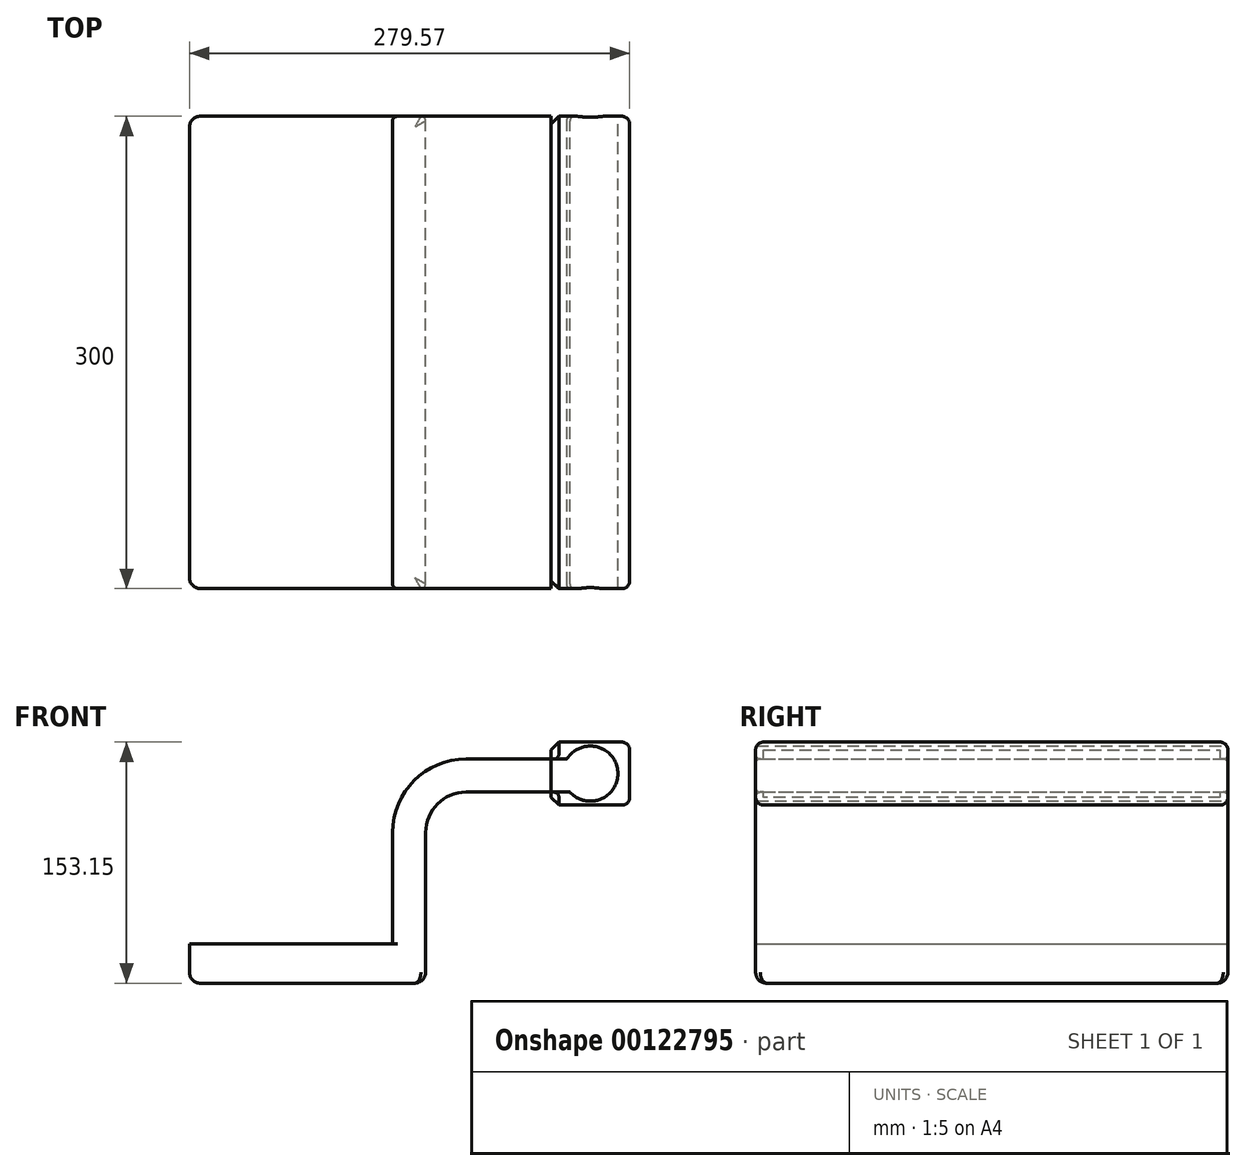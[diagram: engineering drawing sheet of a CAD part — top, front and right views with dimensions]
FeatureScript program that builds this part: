
annotation { "Feature Type Name" : "Feature", "Feature Type Description" : "" }
export const myFeature = defineFeature(function(context is Context, id is Id, definition is map)
    precondition{}
    {
        {
            var Q0;
            Q0=qCreatedBy(makeId("Front.planeOp"),FACE);
            var sketch = newSketch(context, id + "F0", { "sketchPlane" : qUnion([Q0])});
            skLineSegment(sketch, "E0.bottom", {"start": v(20.04, -25.24) * mm, "end": v(-129.96, -25.24) * mm});
            skLineSegment(sketch, "E0.top", {"start": v(20.04, -50.24) * mm, "end": v(-129.96, -50.24) * mm});
            skLineSegment(sketch, "E0.left", {"start": v(20.04, -25.24) * mm, "end": v(20.04, -50.24) * mm});
            skLineSegment(sketch, "E0.right", {"start": v(-129.96, -25.24) * mm, "end": v(-129.96, -50.24) * mm});
            skLineSegment(sketch, "E1.bottom", {"start": v(149.61, 102.9) * mm, "end": v(99.61, 102.9) * mm});
            skLineSegment(sketch, "E1.top", {"start": v(149.61, 62.9) * mm, "end": v(99.61, 62.9) * mm});
            skLineSegment(sketch, "E1.left", {"start": v(149.61, 102.9) * mm, "end": v(149.61, 62.9) * mm});
            skLineSegment(sketch, "E1.right", {"start": v(99.61, 102.9) * mm, "end": v(99.61, 62.9) * mm});
            skLineSegment(sketch, "E2", {"start": v(20.04, -25.24) * mm, "end": v(20.04, 45.54) * mm});
            skArc(sketch, "E3", {"start": v(20.04, 45.54) * mm, "mid": v(27.53, 63.63) * mm, "end": v(45.62, 71.13) * mm});
            skLineSegment(sketch, "E4", {"start": v(45.62, 71.13) * mm, "end": v(115.1, 71.13) * mm});
            skLineSegment(sketch, "E5.0", {"start": v(45.62, 92.13) * mm, "end": v(115.1, 92.13) * mm});
            skArc(sketch, "E5.1", {"start": v(-0.96, 45.54) * mm, "mid": v(12.68, 78.48) * mm, "end": v(45.62, 92.13) * mm});
            skLineSegment(sketch, "E5.2", {"start": v(-0.96, -25.24) * mm, "end": v(-0.96, 45.54) * mm});
            skArc(sketch, "E6", {"start": v(45.62, 92.13) * mm, "mid": v(-59.98, 60.08) * mm, "end": v(-129.96, -25.24) * mm});
            skCircle(sketch, "E7", {"center": v(124.61, 82.9) * mm, "radius": 17.5 * mm});
            skSolve(sketch);
        }
        {
            var Q0;
            Q0=makeQuery(id+"F0.imprint","IMPRINT",FACE,{"disambiguationData":[TD([[makeQuery(id+"F0.imprint","IMPRINT",EDGE,{"derivedFrom":sQuery(id+"F0.wireOp",EDGE,"E0.top")}),-1.0]])]});
            extrude(context, id + "F1", {"entities" : qUnion([Q0]), "depth" : 300 * mm});
        }
        {
            var Q0;
            Q0=makeQuery(id+"F0.imprint","IMPRINT",FACE,{"disambiguationData":[TD([[makeQuery(id+"F0.imprint","IMPRINT",EDGE,{"derivedFrom":sQuery(id+"F0.wireOp",EDGE,"E5.1")}),1.0]])]});
            var Q1;
            {var subQ2=sQuery(id+"F0.wireOp",EDGE,"E2");Q1=makeQuery(id+"F0.imprint","IMPRINT",FACE,{"disambiguationData":[TD([[makeQuery(id+"F0.imprint","IMPRINT",EDGE,{"derivedFrom":subQ2}),1.0]])]});}
            var Q2;
            {var subQ1=sQuery(id+"F0.wireOp",EDGE,"E1.bottom");Q2=makeQuery(id+"F0.imprint","IMPRINT",FACE,{"disambiguationData":[TD([[makeQuery(id+"F0.imprint","IMPRINT",EDGE,{"derivedFrom":subQ1}),1.0]])]});}
            extrude(context, id + "F2", {"entities" : qUnion([Q0, Q1, Q2]), "operationType" : NewBodyOperationType.ADD, "depth" : 300 * mm});
        }
        {
            var Q0;
            Q0=makeQuery(id+"F2.opExtrude","CAP_EDGE",EDGE,{"disambiguationData":[OSD([sQuery(id+"F0.wireOp",EDGE,"E1.left")])],"isStart":false});
            var Q1;
            Q1=makeQuery(id+"F2.opExtrude","CAP_EDGE",EDGE,{"disambiguationData":[OSD([sQuery(id+"F0.wireOp",EDGE,"E1.left")])],"isStart":true});
            var Q2;
            Q2=makeQuery(id+"F2.opExtrude","SWEPT_EDGE",EDGE,{"disambiguationData":[OSD([sQuery(id+"F0.wireOp",EDGE,"E1.bottom"),sQuery(id+"F0.wireOp",EDGE,"E1.left")])]});
            var Q3;
            Q3=makeQuery(id+"F2.opExtrude","SWEPT_EDGE",EDGE,{"disambiguationData":[OSD([sQuery(id+"F0.wireOp",EDGE,"E1.top"),sQuery(id+"F0.wireOp",EDGE,"E1.left")])]});
            var Q4;
            Q4=makeQuery(id+"F2.opExtrude","CAP_EDGE",EDGE,{"disambiguationData":[OSD([sQuery(id+"F0.wireOp",EDGE,"E1.bottom")])],"isStart":false});
            var Q5;
            Q5=makeQuery(id+"F2.opExtrude","CAP_EDGE",EDGE,{"disambiguationData":[OSD([sQuery(id+"F0.wireOp",EDGE,"E1.top")])],"isStart":false});
            var Q6;
            Q6=makeQuery(id+"F2.opExtrude","CAP_EDGE",EDGE,{"disambiguationData":[OSD([sQuery(id+"F0.wireOp",EDGE,"E1.bottom")])],"isStart":true});
            var Q7;
            Q7=makeQuery(id+"F2.opExtrude","CAP_EDGE",EDGE,{"disambiguationData":[OSD([sQuery(id+"F0.wireOp",EDGE,"E1.top")])],"isStart":true});
            fillet(context, id + "F3", {"entities" : qUnion([Q0, Q1, Q2, Q3, Q4, Q5, Q6, Q7]), "radius" : 5 * mm, "tangentPropagation" : true, "allowEdgeOverflow" : false});
        }
        {
            var Q0;
            Q0=makeQuery(id+"F2.opExtrude","SWEPT_EDGE",EDGE,{"disambiguationData":[OSD([sQuery(id+"F0.wireOp",EDGE,"E1.bottom"),sQuery(id+"F0.wireOp",EDGE,"E1.right")])]});
            var Q1;
            Q1=makeQuery(id+"F2.opExtrude","SWEPT_EDGE",EDGE,{"disambiguationData":[OSD([sQuery(id+"F0.wireOp",EDGE,"E1.top"),sQuery(id+"F0.wireOp",EDGE,"E1.right")])]});
            chamfer(context, id + "F4", {"entities" : qUnion([Q0, Q1]), "width" : 5 * mm, "tangentPropagation" : true});
        }
        {
            var Q0;
            Q0=makeQuery(id+"F1.opExtrude","SWEPT_EDGE",EDGE,{"disambiguationData":[OSD([sQuery(id+"F0.wireOp",EDGE,"E0.top"),sQuery(id+"F0.wireOp",EDGE,"E0.right")])]});
            var Q1;
            Q1=makeQuery(id+"F1.opExtrude","CAP_EDGE",EDGE,{"disambiguationData":[OSD([sQuery(id+"F0.wireOp",EDGE,"E0.right")])],"isStart":false});
            var Q2;
            Q2=makeQuery(id+"F1.opExtrude","CAP_EDGE",EDGE,{"disambiguationData":[OSD([sQuery(id+"F0.wireOp",EDGE,"E0.right")])],"isStart":true});
            var Q3;
            Q3=makeQuery(id+"F1.opExtrude","CAP_EDGE",EDGE,{"disambiguationData":[OSD([sQuery(id+"F0.wireOp",EDGE,"E0.top")])],"isStart":false});
            var Q4;
            Q4=makeQuery(id+"F1.opExtrude","SWEPT_EDGE",EDGE,{"disambiguationData":[OSD([sQuery(id+"F0.wireOp",EDGE,"E0.top"),sQuery(id+"F0.wireOp",EDGE,"E0.left")])]});
            var Q5;
            Q5=makeQuery(id+"F1.opExtrude","CAP_EDGE",EDGE,{"disambiguationData":[OSD([sQuery(id+"F0.wireOp",EDGE,"E0.top")])],"isStart":true});
            fillet(context, id + "F5", {"entities" : qUnion([Q0, Q1, Q2, Q3, Q4, Q5]), "radius" : 7 * mm, "tangentPropagation" : true, "allowEdgeOverflow" : false});
        }
        {
            var Q0;
            Q0=makeQuery(id+"F2.opExtrude","CAP_EDGE",EDGE,{"disambiguationData":[OSD([sQuery(id+"F0.wireOp",EDGE,"E4")])],"isStart":false});
            var Q1;
            Q1=makeQuery(id+"F2.opExtrude","CAP_EDGE",EDGE,{"disambiguationData":[OSD([sQuery(id+"F0.wireOp",EDGE,"E3")])],"isStart":false});
            var Q2;
            Q2=makeQuery(id+"F2.boolean.opBoolean","MERGE",EDGE,{"derivedFrom":[makeQuery(id+"F1.opExtrude","CAP_EDGE",EDGE,{"disambiguationData":[OSD([sQuery(id+"F0.wireOp",EDGE,"E0.left")])],"isStart":false}),makeQuery(id+"F2.opExtrude","CAP_EDGE",EDGE,{"disambiguationData":[OSD([sQuery(id+"F0.wireOp",EDGE,"E2")])],"isStart":false})]});
            var Q3;
            Q3=makeQuery(id+"F2.opExtrude","CAP_EDGE",EDGE,{"disambiguationData":[OSD([sQuery(id+"F0.wireOp",EDGE,"E4")])],"isStart":true});
            var Q4;
            Q4=makeQuery(id+"F2.opExtrude","CAP_EDGE",EDGE,{"disambiguationData":[OSD([sQuery(id+"F0.wireOp",EDGE,"E3")])],"isStart":true});
            var Q5;
            Q5=makeQuery(id+"F2.boolean.opBoolean","MERGE",EDGE,{"derivedFrom":[makeQuery(id+"F1.opExtrude","CAP_EDGE",EDGE,{"disambiguationData":[OSD([sQuery(id+"F0.wireOp",EDGE,"E0.left")])],"isStart":true}),makeQuery(id+"F2.opExtrude","CAP_EDGE",EDGE,{"disambiguationData":[OSD([sQuery(id+"F0.wireOp",EDGE,"E2")])],"isStart":true})]});
            fillet(context, id + "F6", {"entities" : qUnion([Q0, Q1, Q2, Q3, Q4, Q5]), "radius" : 3 * mm, "tangentPropagation" : true, "allowEdgeOverflow" : false});
        }
        {
            var Q0;
            Q0=makeQuery(id+"F2.opExtrude","CAP_EDGE",EDGE,{"disambiguationData":[OSD([sQuery(id+"F0.wireOp",EDGE,"E5.0")])],"isStart":true});
            var Q1;
            Q1=makeQuery(id+"F2.opExtrude","CAP_EDGE",EDGE,{"disambiguationData":[OSD([sQuery(id+"F0.wireOp",EDGE,"E6")])],"isStart":true});
            var Q2;
            Q2=makeQuery(id+"F2.opExtrude","CAP_EDGE",EDGE,{"disambiguationData":[OSD([sQuery(id+"F0.wireOp",EDGE,"E5.0")])],"isStart":false});
            var Q3;
            Q3=makeQuery(id+"F2.opExtrude","CAP_EDGE",EDGE,{"disambiguationData":[OSD([sQuery(id+"F0.wireOp",EDGE,"E6")])],"isStart":false});
            fillet(context, id + "F7", {"entities" : qUnion([Q0, Q1, Q2, Q3]), "radius" : 3 * mm, "tangentPropagation" : true, "allowEdgeOverflow" : false});
        }
    });
